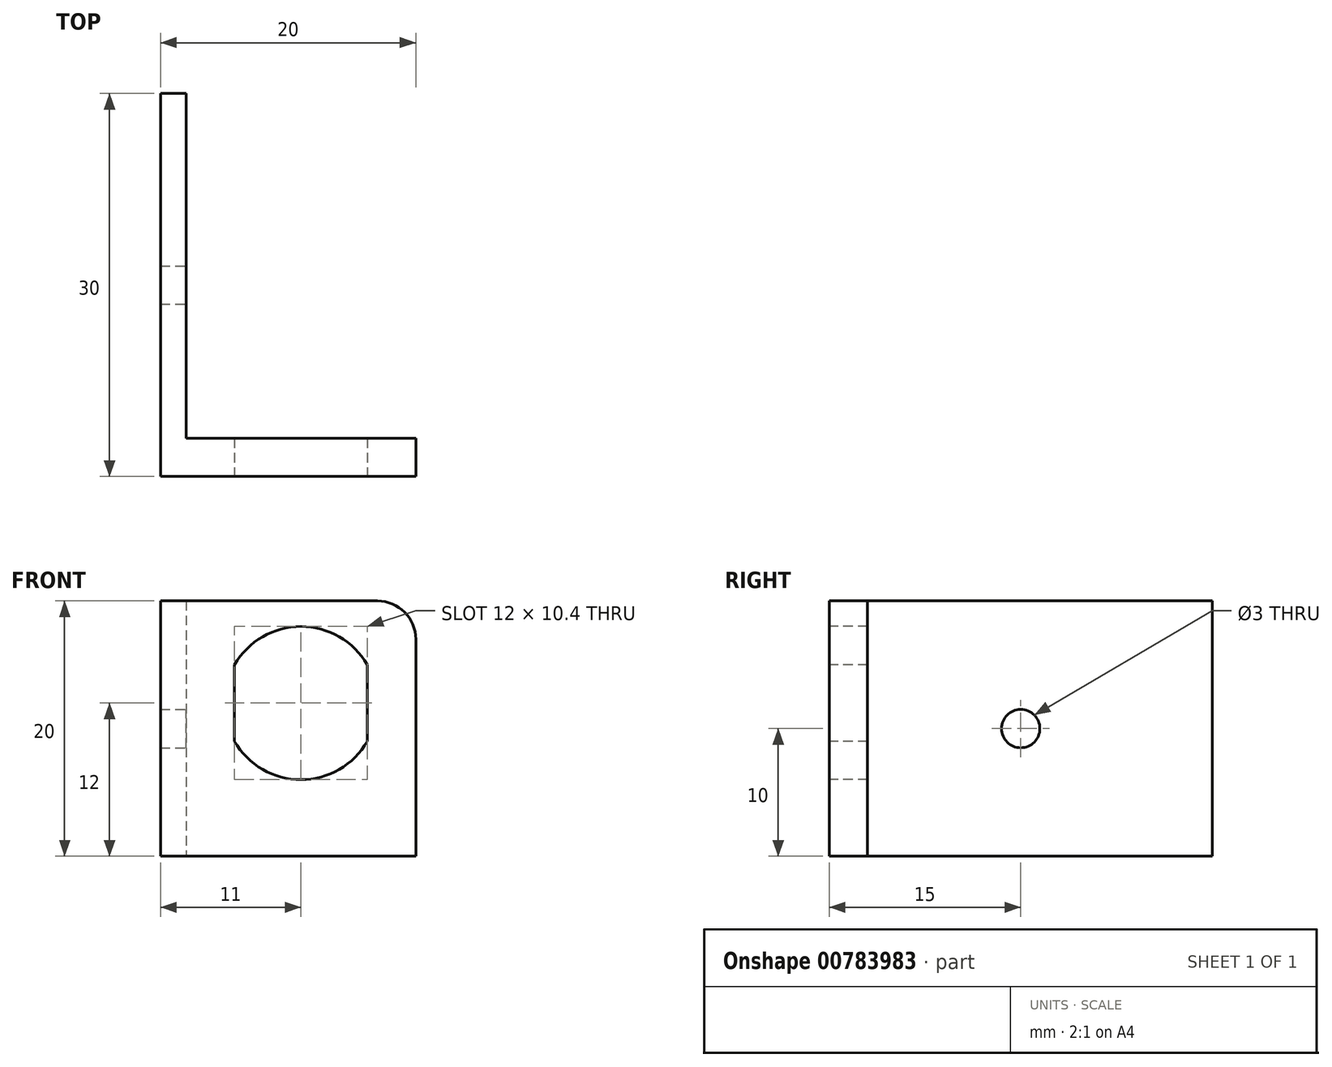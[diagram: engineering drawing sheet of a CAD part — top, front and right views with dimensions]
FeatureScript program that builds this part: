
annotation { "Feature Type Name" : "Feature", "Feature Type Description" : "" }
export const myFeature = defineFeature(function(context is Context, id is Id, definition is map)
    precondition{}
    {
        {
            var Q0;
            Q0=qCreatedBy(makeId("Front.planeOp"),FACE);
            var sketch = newSketch(context, id + "F0", { "sketchPlane" : qUnion([Q0])});
            skLineSegment(sketch, "E0.bottom", {"start": v(0, 0) * mm, "end": v(20, 0) * mm});
            skLineSegment(sketch, "E0.top", {"start": v(0, -20) * mm, "end": v(20, -20) * mm});
            skLineSegment(sketch, "E0.left", {"start": v(0, 0) * mm, "end": v(0, -20) * mm});
            skLineSegment(sketch, "E0.right", {"start": v(20, 0) * mm, "end": v(20, -20) * mm});
            skSolve(sketch);
        }
        {
            var Q0;
            Q0 = qSketchRegion(id + "F0", true);
            extrude(context, id + "F1", {"entities" : qUnion([Q0]), "depth" : 3 * mm, "offsetDistance" : 25 * mm});
        }
        {
            var Q0;
            Q0=makeQuery(id+"F1.opExtrude","CAP_FACE",FACE,{"disambiguationData":[OSD([sQuery(id+"F0.wireOp",EDGE,"E0.bottom"),sQuery(id+"F0.wireOp",EDGE,"E0.top"),sQuery(id+"F0.wireOp",EDGE,"E0.left"),sQuery(id+"F0.wireOp",EDGE,"E0.right")])],"isStart":true});
            var sketch = newSketch(context, id + "F2", { "sketchPlane" : qUnion([Q0])});
            skLineSegment(sketch, "E1.bottom", {"start": v(0, 0) * mm, "end": v(-2, 0) * mm});
            skLineSegment(sketch, "E1.top", {"start": v(0, -20) * mm, "end": v(-2, -20) * mm});
            skLineSegment(sketch, "E1.left", {"start": v(0, 0) * mm, "end": v(0, -20) * mm});
            skLineSegment(sketch, "E1.right", {"start": v(-2, 0) * mm, "end": v(-2, -20) * mm});
            skSolve(sketch);
        }
        {
            var Q0;
            Q0 = qSketchRegion(id + "F2", true);
            extrude(context, id + "F3", {"entities" : qUnion([Q0]), "operationType" : NewBodyOperationType.ADD, "depth" : 27 * mm, "offsetDistance" : 25 * mm});
        }
        {
            var Q0;
            Q0=makeQuery(id+"F1.opExtrude","CAP_FACE",FACE,{"disambiguationData":[OSD([sQuery(id+"F0.wireOp",EDGE,"E0.bottom"),sQuery(id+"F0.wireOp",EDGE,"E0.top"),sQuery(id+"F0.wireOp",EDGE,"E0.left"),sQuery(id+"F0.wireOp",EDGE,"E0.right")])],"isStart":false});
            var sketch = newSketch(context, id + "F4", { "sketchPlane" : qUnion([Q0])});
            skArc(sketch, "E2", {"start": v(5.8, -11) * mm, "mid": v(11, -14) * mm, "end": v(16.2, -11) * mm});
            skLineSegment(sketch, "E3", {"start": v(16.2, -5) * mm, "end": v(16.2, -11) * mm});
            skLineSegment(sketch, "E4", {"start": v(5.8, -5) * mm, "end": v(5.8, -11) * mm});
            skArc(sketch, "E5.trimOffspring", {"start": v(16.2, -5) * mm, "mid": v(11, -2) * mm, "end": v(5.8, -5) * mm});
            skSolve(sketch);
        }
        {
            var Q0;
            Q0=makeQuery(id+"F4.imprint","IMPRINT",FACE,{"disambiguationData":[TD([[makeQuery(id+"F4.imprint","IMPRINT",EDGE,{"derivedFrom":sQuery(id+"F4.wireOp",EDGE,"E2")}),1.0]])]});
            extrude(context, id + "F5", {"entities" : qUnion([Q0]), "operationType" : NewBodyOperationType.REMOVE, "oppositeDirection" : true, "depth" : 25 * mm, "offsetDistance" : 25 * mm});
        }
        {
            var Q0;
            Q0=makeQuery(id+"F3.opExtrude","SWEPT_FACE",FACE,{"disambiguationData":[OSD([sQuery(id+"F2.wireOp",EDGE,"E1.right")])]});
            var sketch = newSketch(context, id + "F6", { "sketchPlane" : qUnion([Q0])});
            skCircle(sketch, "E6", {"center": v(12, -10) * mm, "radius": 1.5 * mm});
            skSolve(sketch);
        }
        {
            var Q0;
            Q0 = qSketchRegion(id + "F6", true);
            extrude(context, id + "F7", {"entities" : qUnion([Q0]), "operationType" : NewBodyOperationType.REMOVE, "oppositeDirection" : true, "depth" : 25 * mm, "offsetDistance" : 25 * mm});
        }
        {
            var Q0;
            Q0=makeQuery(id+"F1.opExtrude","SWEPT_EDGE",EDGE,{"disambiguationData":[OSD([sQuery(id+"F0.wireOp",EDGE,"E0.bottom"),sQuery(id+"F0.wireOp",EDGE,"E0.right")])]});
            fillet(context, id + "F8", {"entities" : qUnion([Q0]), "radius" : 3 * mm, "tangentPropagation" : true, "allowEdgeOverflow" : false});
        }
    });
